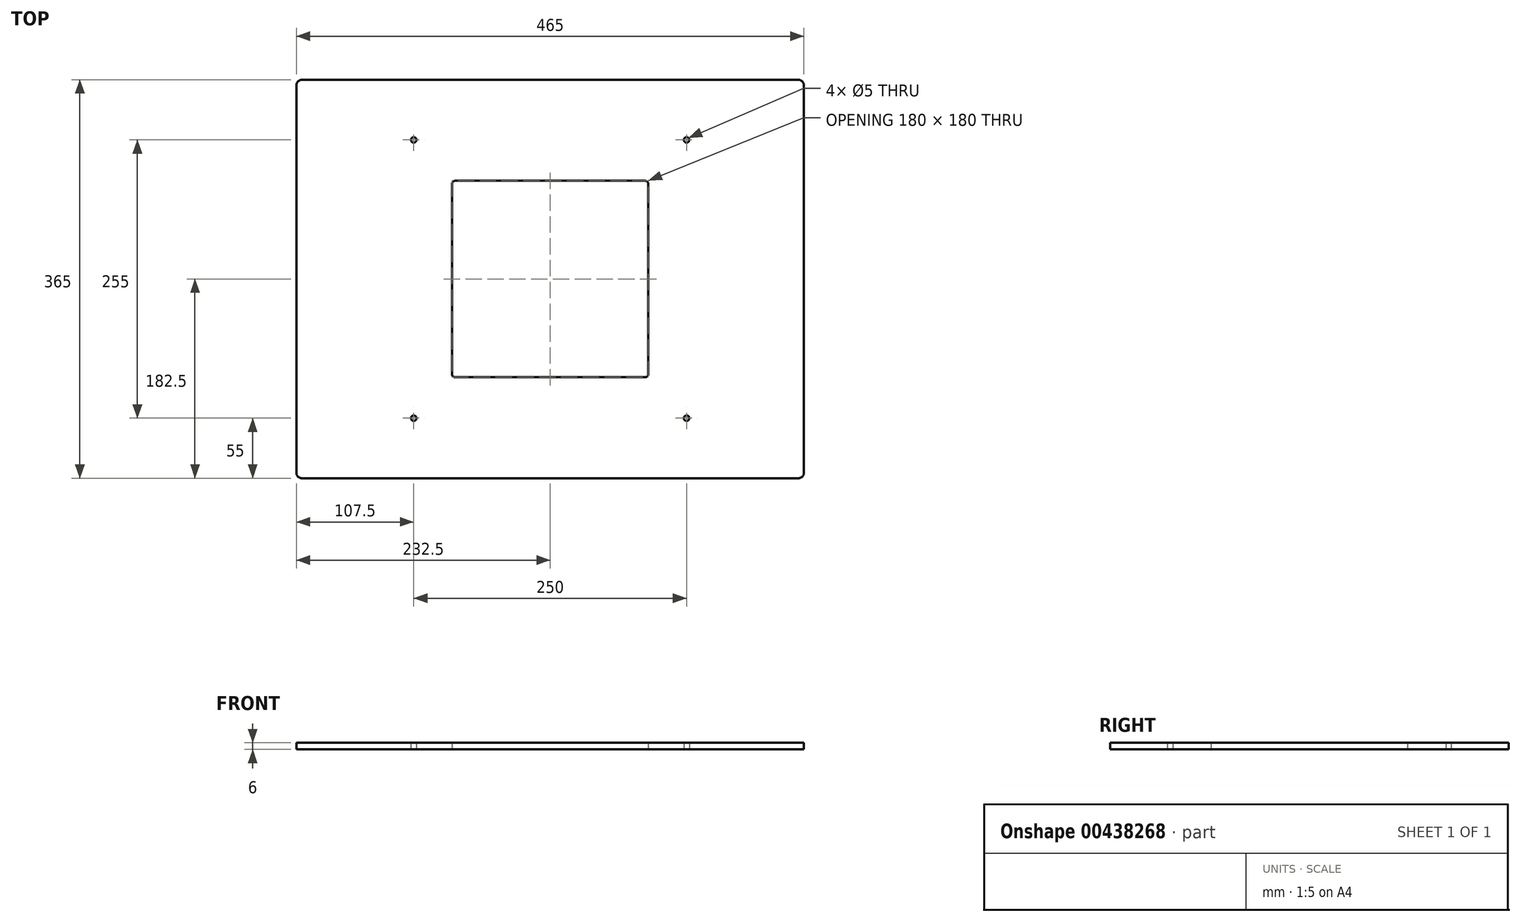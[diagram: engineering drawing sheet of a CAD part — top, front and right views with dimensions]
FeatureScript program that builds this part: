
annotation { "Feature Type Name" : "Feature", "Feature Type Description" : "" }
export const myFeature = defineFeature(function(context is Context, id is Id, definition is map)
    precondition{}
    {
        {
            var Q0;
            Q0=qCreatedBy(makeId("Top.planeOp"),FACE);
            var sketch = newSketch(context, id + "F0", { "sketchPlane" : qUnion([Q0])});
            skLineSegment(sketch, "E0.bottom", {"start": v(-227.5, -182.5) * mm, "end": v(227.5, -182.5) * mm});
            skLineSegment(sketch, "E0.top", {"start": v(-227.5, 182.5) * mm, "end": v(227.5, 182.5) * mm});
            skLineSegment(sketch, "E0.left", {"start": v(-232.5, -177.5) * mm, "end": v(-232.5, 177.5) * mm});
            skLineSegment(sketch, "E0.right", {"start": v(232.5, -177.5) * mm, "end": v(232.5, 177.5) * mm});
            skPoint(sketch, "E0.middle", {"position": v(0, 0) * mm});
            skLineSegment(sketch, "E1.bottom", {"start": v(-87, -90) * mm, "end": v(87, -90) * mm});
            skLineSegment(sketch, "E1.top", {"start": v(-87, 90) * mm, "end": v(87, 90) * mm});
            skLineSegment(sketch, "E1.left", {"start": v(-90, -87) * mm, "end": v(-90, 87) * mm});
            skLineSegment(sketch, "E1.right", {"start": v(90, -87) * mm, "end": v(90, 87) * mm});
            skPoint(sketch, "E2.visualSharp", {"position": v(90, -90) * mm});
            skArc(sketch, "E2.filletArc", {"start": v(87, -90) * mm, "mid": v(89.12, -89.12) * mm, "end": v(90, -87) * mm});
            skPoint(sketch, "E3.visualSharp", {"position": v(-90, -90) * mm});
            skArc(sketch, "E3.filletArc", {"start": v(-90, -87) * mm, "mid": v(-89.12, -89.12) * mm, "end": v(-87, -90) * mm});
            skPoint(sketch, "E4.visualSharp", {"position": v(-90, 90) * mm});
            skArc(sketch, "E4.filletArc", {"start": v(-87, 90) * mm, "mid": v(-89.12, 89.12) * mm, "end": v(-90, 87) * mm});
            skPoint(sketch, "E5.visualSharp", {"position": v(90, 90) * mm});
            skArc(sketch, "E5.filletArc", {"start": v(90, 87) * mm, "mid": v(89.12, 89.12) * mm, "end": v(87, 90) * mm});
            skPoint(sketch, "E6.visualSharp", {"position": v(-232.5, -182.5) * mm});
            skArc(sketch, "E6.filletArc", {"start": v(-232.5, -177.5) * mm, "mid": v(-231.04, -181.04) * mm, "end": v(-227.5, -182.5) * mm});
            skPoint(sketch, "E7.visualSharp", {"position": v(-232.5, 182.5) * mm});
            skArc(sketch, "E7.filletArc", {"start": v(-227.5, 182.5) * mm, "mid": v(-231.04, 181.04) * mm, "end": v(-232.5, 177.5) * mm});
            skPoint(sketch, "E8.visualSharp", {"position": v(232.5, 182.5) * mm});
            skArc(sketch, "E8.filletArc", {"start": v(232.5, 177.5) * mm, "mid": v(231.04, 181.04) * mm, "end": v(227.5, 182.5) * mm});
            skPoint(sketch, "E9.visualSharp", {"position": v(232.5, -182.5) * mm});
            skArc(sketch, "E9.filletArc", {"start": v(227.5, -182.5) * mm, "mid": v(231.04, -181.04) * mm, "end": v(232.5, -177.5) * mm});
            skSolve(sketch);
        }
        {
            var Q0;
            Q0 = qSketchRegion(id + "F0", true);
            extrude(context, id + "F1", {"entities" : qUnion([Q0]), "depth" : 6 * mm});
        }
        {
            var Q0;
            Q0=makeQuery(id+"F1.opExtrude","CAP_FACE",FACE,{"disambiguationData":[OSD([sQuery(id+"F0.wireOp",EDGE,"E0.bottom"),sQuery(id+"F0.wireOp",EDGE,"E0.top"),sQuery(id+"F0.wireOp",EDGE,"E0.left"),sQuery(id+"F0.wireOp",EDGE,"E0.right"),sQuery(id+"F0.wireOp",EDGE,"E1.bottom"),sQuery(id+"F0.wireOp",EDGE,"E1.top"),sQuery(id+"F0.wireOp",EDGE,"E1.left"),sQuery(id+"F0.wireOp",EDGE,"E1.right"),sQuery(id+"F0.wireOp",EDGE,"E2.filletArc"),sQuery(id+"F0.wireOp",EDGE,"E3.filletArc"),sQuery(id+"F0.wireOp",EDGE,"E4.filletArc"),sQuery(id+"F0.wireOp",EDGE,"E5.filletArc"),sQuery(id+"F0.wireOp",EDGE,"E6.filletArc"),sQuery(id+"F0.wireOp",EDGE,"E7.filletArc"),sQuery(id+"F0.wireOp",EDGE,"E8.filletArc"),sQuery(id+"F0.wireOp",EDGE,"E9.filletArc")])],"isStart":false});
            var sketch = newSketch(context, id + "F2", { "sketchPlane" : qUnion([Q0])});
            skPoint(sketch, "E10", {"position": v(125, -127.5) * mm});
            skLineSegment(sketch, "E11", {"start": v(0, 0) * mm, "end": v(0, -182.5) * mm, "construction": true});
            skLineSegment(sketch, "E12", {"start": v(0, 0) * mm, "end": v(232.5, 0) * mm, "construction": true});
            skPoint(sketch, "E13.MirrorP", {"position": v(-125, -127.5) * mm});
            skPoint(sketch, "E14.MirrorP", {"position": v(125, 127.5) * mm});
            skPoint(sketch, "E15.MirrorP", {"position": v(-125, 127.5) * mm});
            skSolve(sketch);
        }
        {
            var Q0;
            Q0=sQuery(id+"F2.wireOp",VERTEX,"E10");
            var Q1;
            Q1=sQuery(id+"F2.wireOp",VERTEX,"E13.MirrorP");
            var Q2;
            Q2=sQuery(id+"F2.wireOp",VERTEX,"E14.MirrorP");
            var Q3;
            Q3=sQuery(id+"F2.wireOp",VERTEX,"E15.MirrorP");
            var Q4;
            Q4=makeQuery(id+"F1.opExtrude","SWEPT_BODY",BODY,{"disambiguationData":[OSD([sQuery(id+"F0.wireOp",EDGE,"E0.bottom"),sQuery(id+"F0.wireOp",EDGE,"E0.top"),sQuery(id+"F0.wireOp",EDGE,"E0.left"),sQuery(id+"F0.wireOp",EDGE,"E0.right"),sQuery(id+"F0.wireOp",EDGE,"E1.bottom"),sQuery(id+"F0.wireOp",EDGE,"E1.top"),sQuery(id+"F0.wireOp",EDGE,"E1.left"),sQuery(id+"F0.wireOp",EDGE,"E1.right"),sQuery(id+"F0.wireOp",EDGE,"E2.filletArc"),sQuery(id+"F0.wireOp",EDGE,"E3.filletArc"),sQuery(id+"F0.wireOp",EDGE,"E4.filletArc"),sQuery(id+"F0.wireOp",EDGE,"E5.filletArc"),sQuery(id+"F0.wireOp",EDGE,"E6.filletArc"),sQuery(id+"F0.wireOp",EDGE,"E7.filletArc"),sQuery(id+"F0.wireOp",EDGE,"E8.filletArc"),sQuery(id+"F0.wireOp",EDGE,"E9.filletArc")])]});
            hole(context, id + "F3", {"style" : HoleStyle.SIMPLE, "endStyle" : HoleEndStyle.THROUGH, "holeDiameter" : 5 * mm, "isTappedThrough" : true, "tappedDepth" : 12 * mm, "tapClearance" : 3, "locations" : qUnion([Q0, Q1, Q2, Q3]), "scope" : qUnion([Q4]), "startStyle" : HoleStartStyle.PART});
        }
    });
